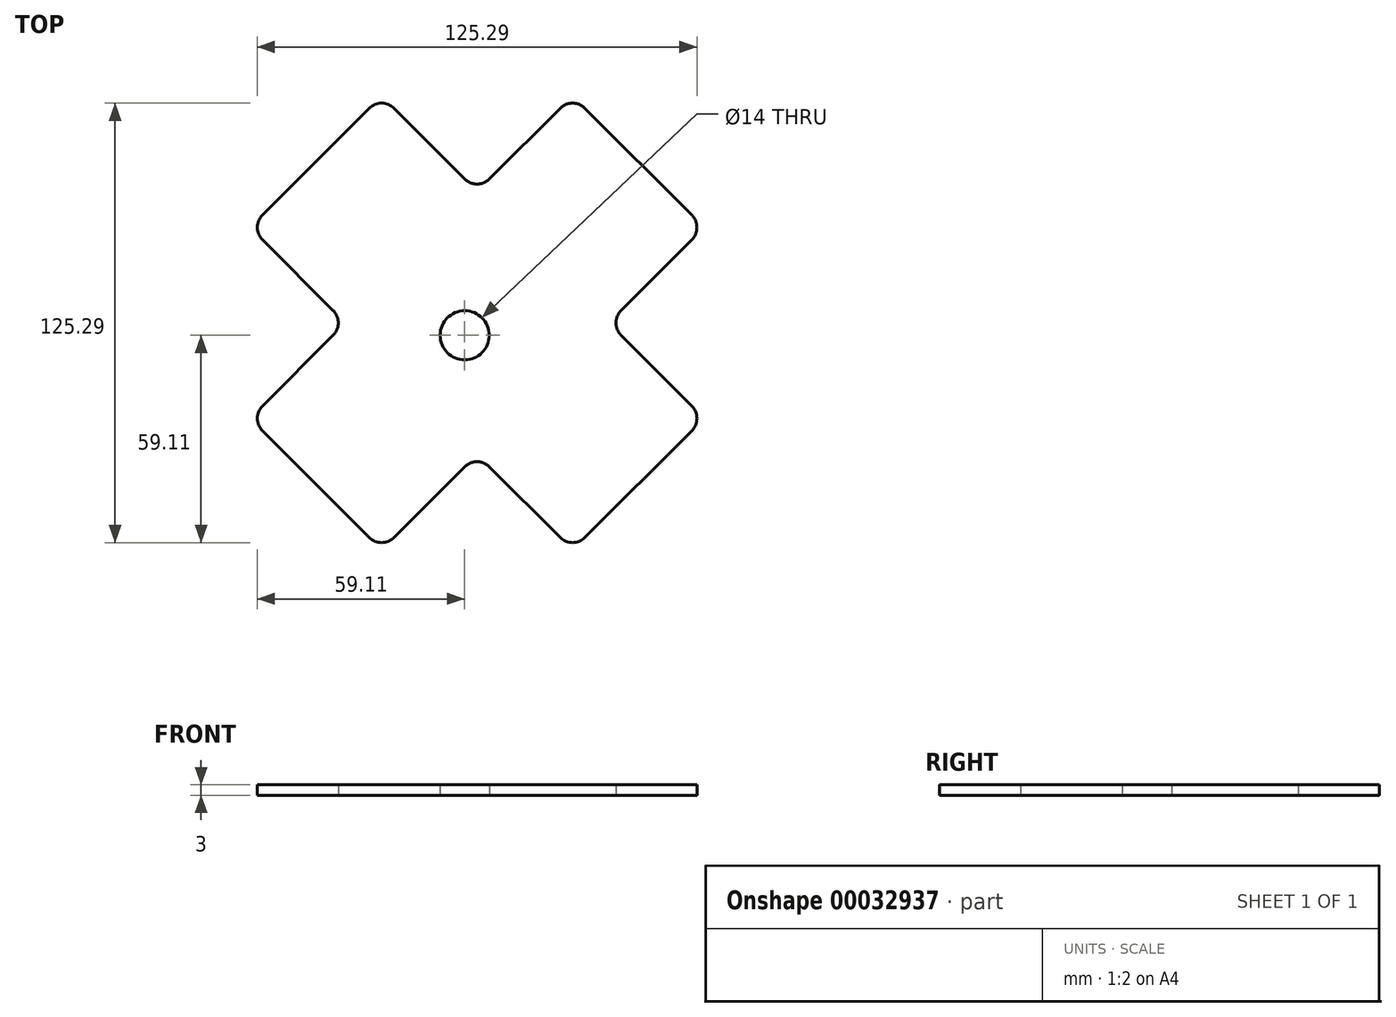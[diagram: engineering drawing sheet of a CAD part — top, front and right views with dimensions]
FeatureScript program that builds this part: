
annotation { "Feature Type Name" : "Feature", "Feature Type Description" : "" }
export const myFeature = defineFeature(function(context is Context, id is Id, definition is map)
    precondition{}
    {
        {
            var Q0;
            Q0=qCreatedBy(makeId("Top.planeOp"),FACE);
            var sketch = newSketch(context, id + "F0", { "sketchPlane" : qUnion([Q0])});
            skPoint(sketch, "E0.rect.middle", {"position": v(0, 0) * mm});
            skPoint(sketch, "E1.0.midPoint", {"position": v(0, 42.25) * mm});
            skCircle(sketch, "E2", {"center": v(0, 0) * mm, "radius": 7 * mm});
            skLineSegment(sketch, "E3.MirrorCS", {"start": v(44.57, 7.07) * mm, "end": v(64.71, 27.21) * mm});
            skLineSegment(sketch, "E4", {"start": v(34.28, 64.71) * mm, "end": v(64.71, 34.28) * mm});
            skPoint(sketch, "E5.visualSharp", {"position": v(30.75, 68.25) * mm});
            skArc(sketch, "E5.filletArc", {"start": v(34.28, 64.71) * mm, "mid": v(30.75, 66.18) * mm, "end": v(27.21, 64.71) * mm});
            skPoint(sketch, "E6.visualSharp", {"position": v(68.25, 30.75) * mm});
            skArc(sketch, "E6.filletArc", {"start": v(64.71, 27.21) * mm, "mid": v(66.18, 30.75) * mm, "end": v(64.71, 34.28) * mm});
            skLineSegment(sketch, "E7.1.0", {"start": v(-37.5, 7.07) * mm, "end": v(-57.64, 27.21) * mm});
            skArc(sketch, "E7.1.1", {"start": v(-57.64, 34.28) * mm, "mid": v(-59.1, 30.75) * mm, "end": v(-57.64, 27.21) * mm});
            skLineSegment(sketch, "E7.1.2", {"start": v(-57.64, 34.28) * mm, "end": v(-27.21, 64.71) * mm});
            skArc(sketch, "E7.1.3", {"start": v(-20.14, 64.71) * mm, "mid": v(-23.68, 66.18) * mm, "end": v(-27.21, 64.71) * mm});
            skLineSegment(sketch, "E7.1.4", {"start": v(0, 44.57) * mm, "end": v(-20.14, 64.71) * mm});
            skLineSegment(sketch, "E7.2.0", {"start": v(0, -37.5) * mm, "end": v(-20.14, -57.64) * mm});
            skArc(sketch, "E7.2.1", {"start": v(-27.21, -57.64) * mm, "mid": v(-23.68, -59.1) * mm, "end": v(-20.14, -57.64) * mm});
            skLineSegment(sketch, "E7.2.2", {"start": v(-27.21, -57.64) * mm, "end": v(-57.64, -27.21) * mm});
            skArc(sketch, "E7.2.3", {"start": v(-57.64, -20.14) * mm, "mid": v(-59.1, -23.68) * mm, "end": v(-57.64, -27.21) * mm});
            skLineSegment(sketch, "E7.2.4", {"start": v(-37.5, 0) * mm, "end": v(-57.64, -20.14) * mm});
            skLineSegment(sketch, "E7.3.0", {"start": v(44.57, 0) * mm, "end": v(64.71, -20.14) * mm});
            skArc(sketch, "E7.3.1", {"start": v(64.71, -27.21) * mm, "mid": v(66.18, -23.68) * mm, "end": v(64.71, -20.14) * mm});
            skLineSegment(sketch, "E7.3.2", {"start": v(64.71, -27.21) * mm, "end": v(34.28, -57.64) * mm});
            skArc(sketch, "E7.3.3", {"start": v(27.21, -57.64) * mm, "mid": v(30.75, -59.1) * mm, "end": v(34.28, -57.64) * mm});
            skLineSegment(sketch, "E7.3.4", {"start": v(7.07, -37.5) * mm, "end": v(27.21, -57.64) * mm});
            skLineSegment(sketch, "E8.trimOffspring", {"start": v(7.07, 44.57) * mm, "end": v(27.21, 64.71) * mm});
            skArc(sketch, "E9.filletArc", {"start": v(0, 44.57) * mm, "mid": v(3.54, 43.1) * mm, "end": v(7.07, 44.57) * mm});
            skArc(sketch, "E10.filletArc", {"start": v(44.57, 7.07) * mm, "mid": v(43.1, 3.54) * mm, "end": v(44.57, 0) * mm});
            skArc(sketch, "E11.filletArc", {"start": v(7.07, -37.5) * mm, "mid": v(3.54, -36.04) * mm, "end": v(0, -37.5) * mm});
            skPoint(sketch, "E12.visualSharp", {"position": v(-33.96, 3.54) * mm});
            skArc(sketch, "E12.filletArc", {"start": v(-37.5, 0) * mm, "mid": v(-36.04, 3.54) * mm, "end": v(-37.5, 7.07) * mm});
            skSolve(sketch);
        }
        {
            var Q0;
            Q0=makeQuery(id+"F0.imprint","IMPRINT",FACE,{"disambiguationData":[TD([[makeQuery(id+"F0.imprint","IMPRINT",EDGE,{"derivedFrom":sQuery(id+"F0.wireOp",EDGE,"E2")}),-1.0]])]});
            extrude(context, id + "F1", {"entities" : qUnion([Q0]), "depth" : 3 * mm});
        }
    });
